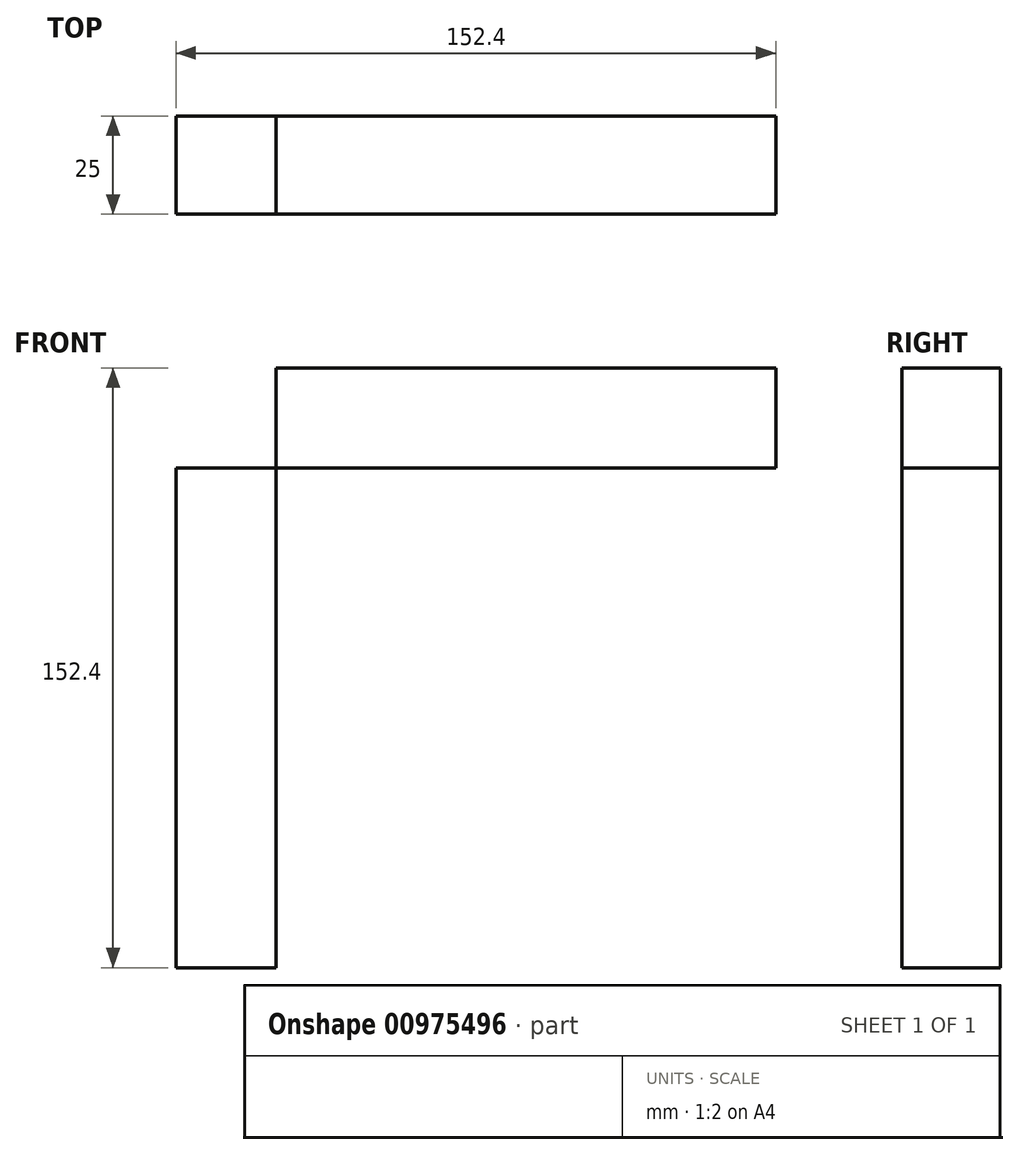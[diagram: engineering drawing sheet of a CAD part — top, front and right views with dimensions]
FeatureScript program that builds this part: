
annotation { "Feature Type Name" : "Feature", "Feature Type Description" : "" }
export const myFeature = defineFeature(function(context is Context, id is Id, definition is map)
    precondition{}
    {
        {
            var Q0;
            Q0=qCreatedBy(makeId("Front.planeOp"),FACE);
            var sketch = newSketch(context, id + "F0", { "sketchPlane" : qUnion([Q0])});
            skLineSegment(sketch, "E0.bottom", {"start": v(-61.27, 94.47) * mm, "end": v(-35.87, 94.47) * mm});
            skLineSegment(sketch, "E0.top", {"start": v(-61.27, -57.93) * mm, "end": v(-35.87, -57.93) * mm});
            skLineSegment(sketch, "E0.left", {"start": v(-61.27, 94.47) * mm, "end": v(-61.27, -57.93) * mm});
            skLineSegment(sketch, "E0.right", {"start": v(-35.87, 94.47) * mm, "end": v(-35.87, -57.93) * mm});
            skLineSegment(sketch, "E1.bottom", {"start": v(-61.27, 94.47) * mm, "end": v(91.13, 94.47) * mm});
            skLineSegment(sketch, "E1.top", {"start": v(-61.27, 69.07) * mm, "end": v(91.13, 69.07) * mm});
            skLineSegment(sketch, "E1.left", {"start": v(-61.27, 94.47) * mm, "end": v(-61.27, 69.07) * mm});
            skLineSegment(sketch, "E1.right", {"start": v(91.13, 94.47) * mm, "end": v(91.13, 69.07) * mm});
            skSolve(sketch);
        }
        {
            var Q0;
            {var subQ5=sQuery(id+"F0.wireOp",EDGE,"E1.left");Q0=makeQuery(id+"F0.imprint","IMPRINT",FACE,{"disambiguationData":[TD([[makeQuery(id+"F0.imprint","IMPRINT",EDGE,{"derivedFrom":subQ5}),1.0]])]});}
            var Q1;
            {var subQ0=sQuery(id+"F0.wireOp",EDGE,"E0.top");Q1=makeQuery(id+"F0.imprint","IMPRINT",FACE,{"disambiguationData":[TD([[makeQuery(id+"F0.imprint","IMPRINT",EDGE,{"derivedFrom":subQ0}),1.0]])]});}
            var Q2;
            {var subQ5=sQuery(id+"F0.wireOp",EDGE,"E1.right");Q2=makeQuery(id+"F0.imprint","IMPRINT",FACE,{"disambiguationData":[TD([[makeQuery(id+"F0.imprint","IMPRINT",EDGE,{"derivedFrom":subQ5}),-1.0]])]});}
            extrude(context, id + "F1", {"entities" : qUnion([Q0, Q1, Q2]), "depth" : 25 * mm, "offsetDistance" : 25 * mm});
        }
    });
